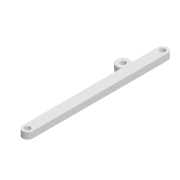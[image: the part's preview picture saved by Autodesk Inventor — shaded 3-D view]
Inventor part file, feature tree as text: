
AUTODESK INVENTOR PART (.ipt)
format: ipt  version: 2022 (Build 260153000, 153)  size: 97,792 bytes
history: native  units: mm
features: extrude x1, sketch x1
ambient origin geometry x8: Origin, YZ Plane, XZ Plane, XY Plane, X Axis, Y Axis, Z Axis, Center Point
bodies: Solid1 (feature_tree)
feature tree (2):
  extrude  "Extrusion1"  Depth=8.0mm
  sketch  "Sketch1"  dims[d0=110.0mm d1=8.0mm d2=4.2mm d3=4.2mm d4=5.0mm d5=0.0mm d6=4.2mm d9=85.0mm d10=3.0mm d11=10.0mm]
